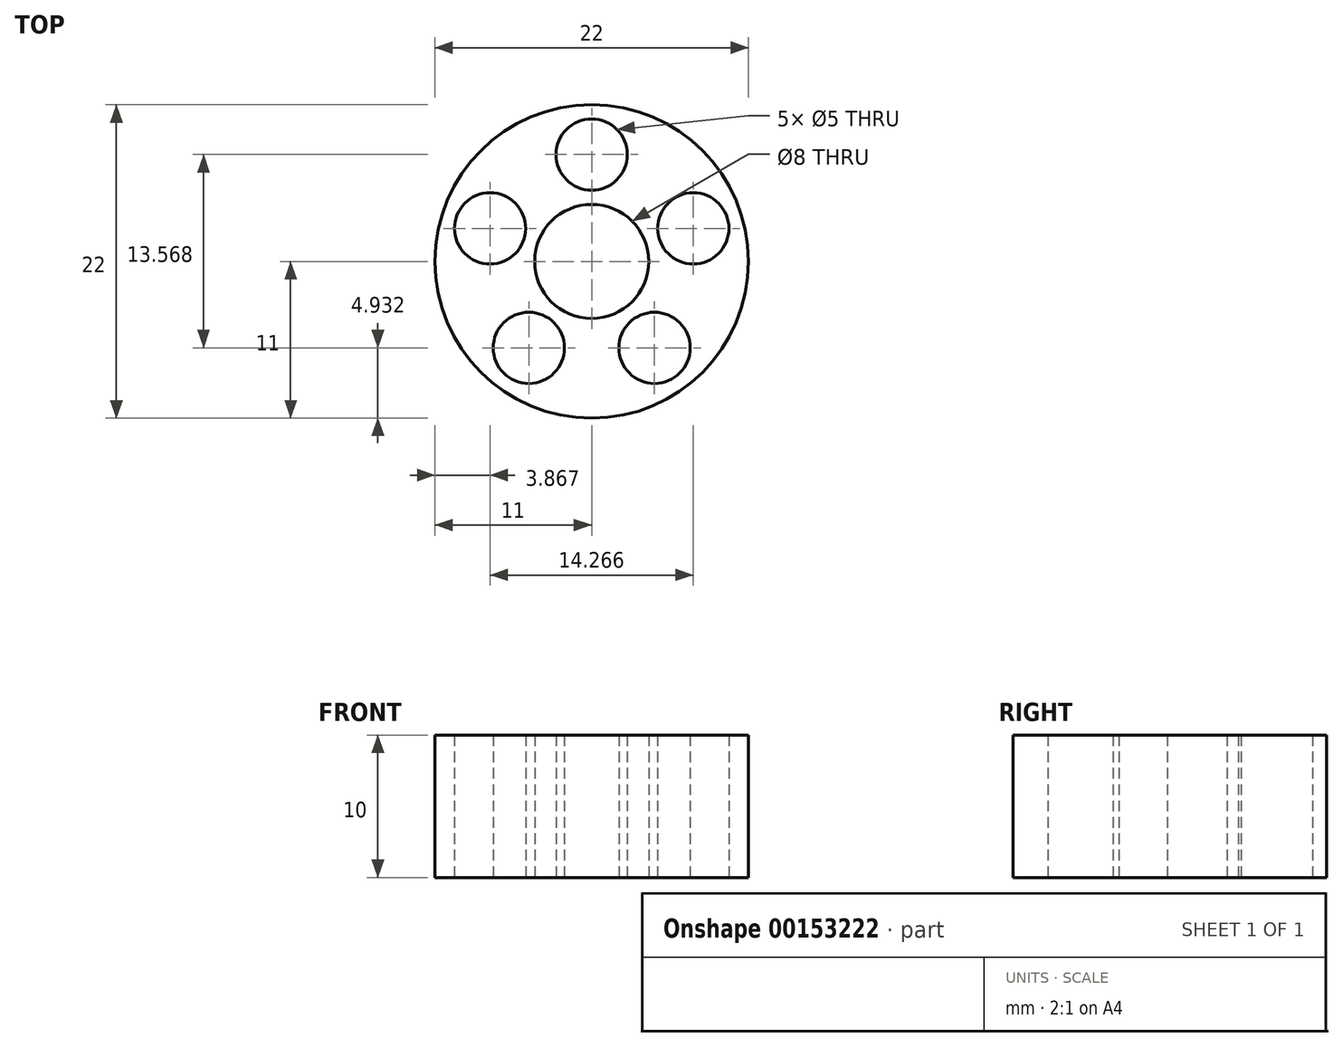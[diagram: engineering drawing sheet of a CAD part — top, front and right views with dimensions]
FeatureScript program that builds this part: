
annotation { "Feature Type Name" : "Feature", "Feature Type Description" : "" }
export const myFeature = defineFeature(function(context is Context, id is Id, definition is map)
    precondition{}
    {
        {
            var Q0;
            Q0=qCreatedBy(makeId("Top.planeOp"),FACE);
            var sketch = newSketch(context, id + "F0", { "sketchPlane" : qUnion([Q0])});
            skCircle(sketch, "E0", {"center": v(0, 0) * mm, "radius": 11 * mm});
            skCircle(sketch, "E1", {"center": v(0, 0) * mm, "radius": 4 * mm});
            skCircle(sketch, "E2", {"center": v(0, 7.5) * mm, "radius": 2.5 * mm});
            skCircle(sketch, "E3", {"center": v(0, 0) * mm, "radius": 7.5 * mm, "construction": true});
            skLineSegment(sketch, "E4.0", {"start": v(0, 7.5) * mm, "end": v(7.13, 2.32) * mm, "construction": true});
            skLineSegment(sketch, "E4.1", {"start": v(7.13, 2.32) * mm, "end": v(4.4, -6.07) * mm, "construction": true});
            skLineSegment(sketch, "E4.2", {"start": v(4.4, -6.07) * mm, "end": v(-4.4, -6.07) * mm, "construction": true});
            skLineSegment(sketch, "E4.3", {"start": v(-4.4, -6.07) * mm, "end": v(-7.13, 2.32) * mm, "construction": true});
            skLineSegment(sketch, "E4.4", {"start": v(-7.13, 2.32) * mm, "end": v(0, 7.5) * mm, "construction": true});
            skCircle(sketch, "E5", {"center": v(-7.13, 2.32) * mm, "radius": 2.5 * mm});
            skCircle(sketch, "E6", {"center": v(4.4, -6.07) * mm, "radius": 2.5 * mm});
            skCircle(sketch, "E7", {"center": v(7.13, 2.32) * mm, "radius": 2.5 * mm});
            skCircle(sketch, "E8", {"center": v(-4.4, -6.07) * mm, "radius": 2.5 * mm});
            skSolve(sketch);
        }
        {
            var Q0;
            Q0 = qSketchRegion(id + "F0", true);
            extrude(context, id + "F1", {"entities" : qUnion([Q0]), "depth" : 10 * mm});
        }
    });
